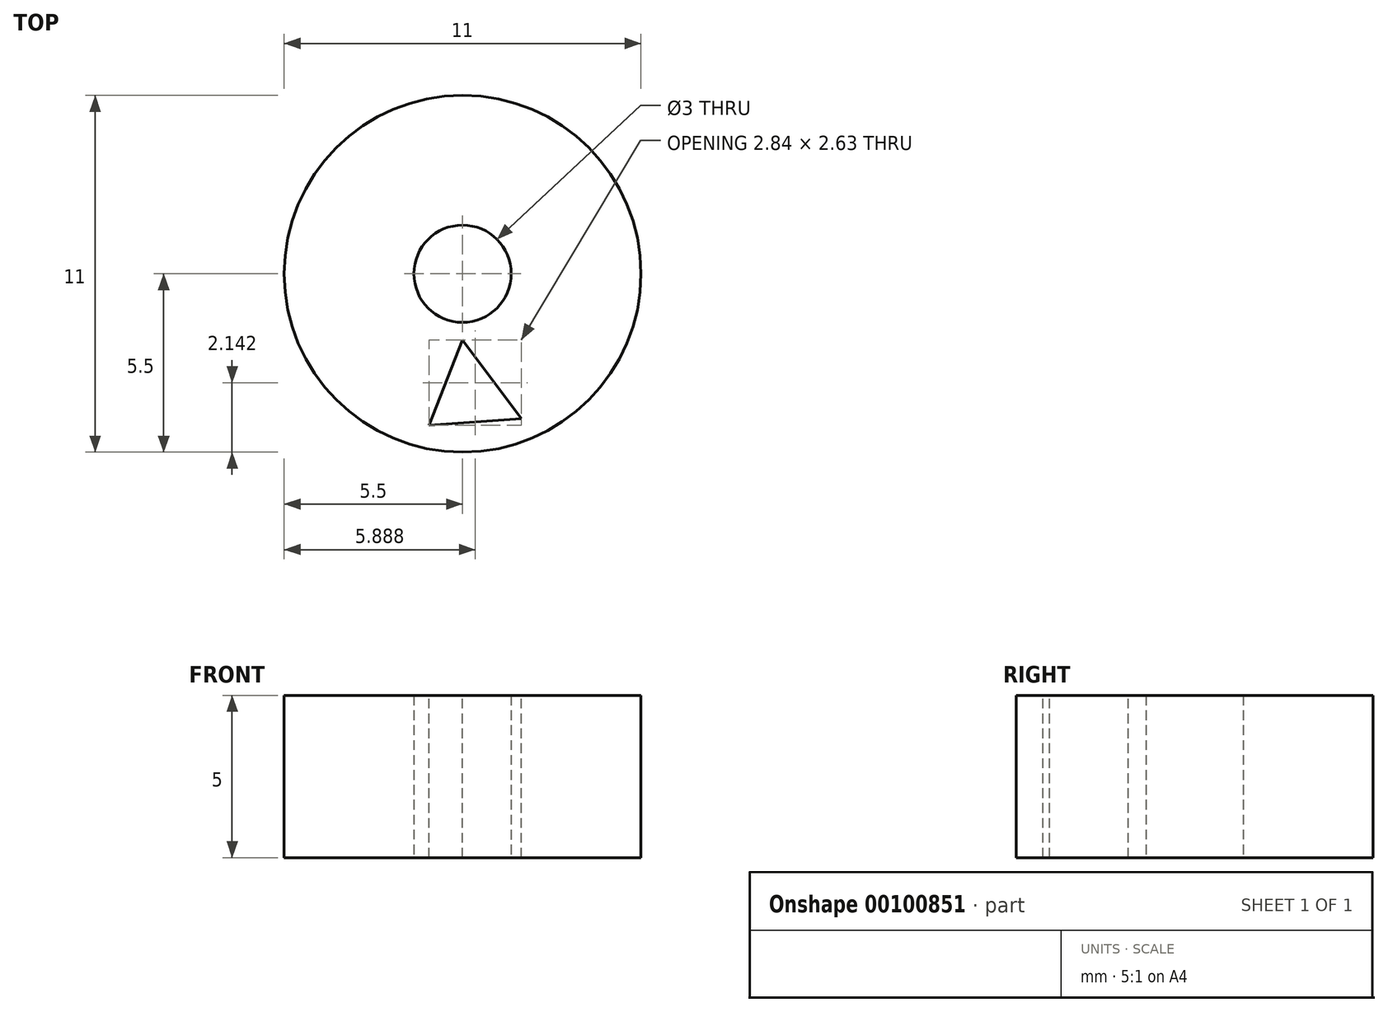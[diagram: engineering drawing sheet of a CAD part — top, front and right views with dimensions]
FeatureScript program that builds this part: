
annotation { "Feature Type Name" : "Feature", "Feature Type Description" : "" }
export const myFeature = defineFeature(function(context is Context, id is Id, definition is map)
    precondition{}
    {
        {
            var Q0;
            Q0=qCreatedBy(makeId("Top.planeOp"),FACE);
            var sketch = newSketch(context, id + "F0", { "sketchPlane" : qUnion([Q0])});
            skCircle(sketch, "E0", {"center": v(0, 0) * mm, "radius": 5.5 * mm});
            skCircle(sketch, "E1", {"center": v(0, 0) * mm, "radius": 1.5 * mm});
            skSolve(sketch);
        }
        {
            var Q0;
            Q0=qSketchRegion(id+"F0",true);
            extrude(context, id + "F1", {"entities" : qUnion([Q0]), "depth" : 5 * mm});
        }
        {
            var Q0;
            Q0=makeQuery(id+"F1.opExtrude","CAP_FACE",FACE,{"disambiguationData":[OSD([sQuery(id+"F0.wireOp",EDGE,"E0"),sQuery(id+"F0.wireOp",EDGE,"E1")])],"isStart":false});
            var sketch = newSketch(context, id + "F2", { "sketchPlane" : qUnion([Q0])});
            skPoint(sketch, "E2.middle", {"position": v(0, 0) * mm});
            skLineSegment(sketch, "E3", {"start": v(0, -2.04) * mm, "end": v(-1.03, -4.67) * mm});
            skLineSegment(sketch, "E4", {"start": v(-1.03, -4.67) * mm, "end": v(1.8, -4.46) * mm});
            skLineSegment(sketch, "E5", {"start": v(1.8, -4.46) * mm, "end": v(0, -2.04) * mm});
            skSolve(sketch);
        }
        {
            var Q0;
            Q0=makeQuery(id+"F2.imprint","IMPRINT",FACE,{"disambiguationData":[TD([[makeQuery(id+"F2.imprint","IMPRINT",EDGE,{"derivedFrom":sQuery(id+"F2.wireOp",EDGE,"E3")}),1.0]])]});
            extrude(context, id + "F3", {"entities" : qUnion([Q0]), "operationType" : NewBodyOperationType.REMOVE, "oppositeDirection" : true, "depth" : 5 * mm});
        }
    });
